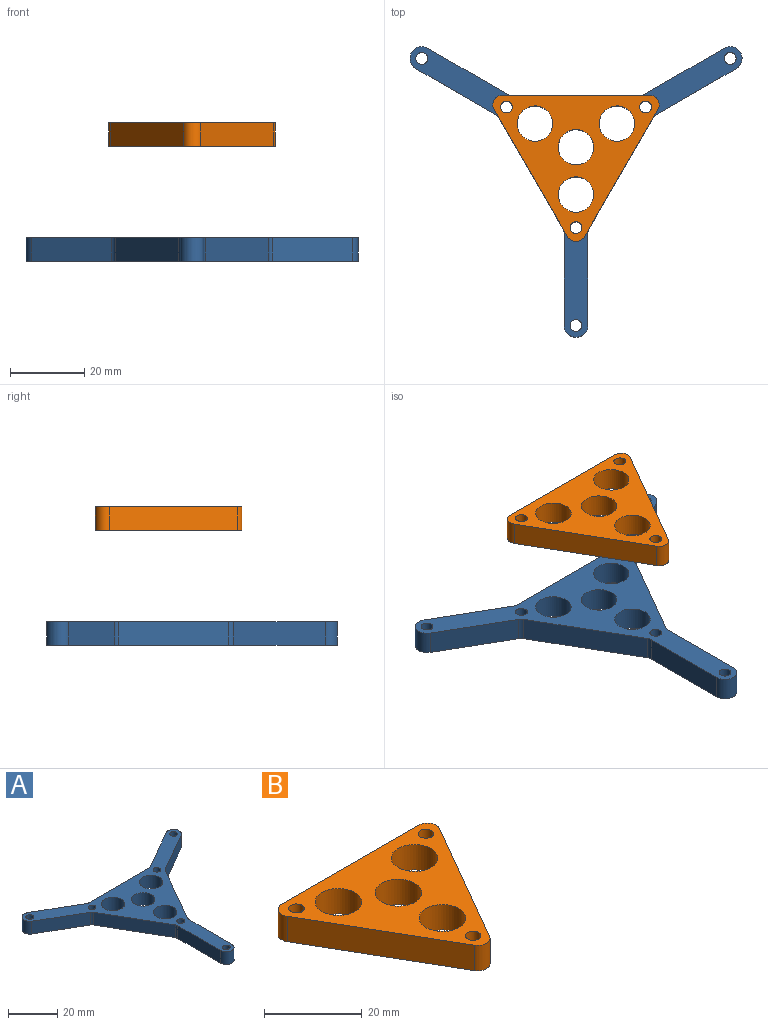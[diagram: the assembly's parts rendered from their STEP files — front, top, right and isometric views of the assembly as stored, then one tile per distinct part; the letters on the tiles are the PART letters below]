
ASSEMBLY  parts=2 mates=2
PART A: 30 faces, bbox 89.2x78.1x6.4 mm
  f0: plane 24.72x6.35mm, normal (1,0,0), area 157mm2, adj f19,f22,f23,f25
  f1: plane 29.73x17.17mm, normal (0.87,-0.5,0), area 218mm2, adj f22,f23,f25,f29
  f2: plane 21.41x12.36mm, normal (0.5,-0.87,0), area 157mm2, adj f3,f22,f23,f29
  f3: cylinder r=3.17mm len=6.35mm, axis (0,0,-1), area 63.3mm2, adj f2,f4,f22,f23
  f4: plane 21.41x12.36mm, normal (-0.5,0.87,0), area 157mm2, adj f3,f22,f23,f28
  f5: plane 34.33x6.35mm, normal (0,1,0), area 218mm2, adj f22,f23,f27,f28
  f6: plane 21.41x12.36mm, normal (0.5,0.87,0), area 157mm2, adj f7,f22,f23,f27
  f7: cylinder r=3.17mm len=6.35mm, axis (0,0,-1), area 63.3mm2, adj f6,f8,f22,f23
  f8: plane 21.41x12.36mm, normal (-0.5,-0.87,0), area 157mm2, adj f7,f22,f23,f26
  f9: plane 29.73x17.17mm, normal (-0.87,-0.5,0), area 218mm2, adj f22,f23,f24,f26
  f10: plane 24.72x6.35mm, normal (-1,0,0), area 157mm2, adj f19,f22,f23,f24
  f11: cylinder r=1.59mm len=6.35mm, axis (0,0,-1), area 63.3mm2, adj f22,f23
  f12: cylinder r=1.59mm len=6.35mm, axis (0,0,-1), area 63.3mm2, adj f22,f23
  f13: cylinder r=1.59mm len=6.35mm, axis (0,0,-1), area 63.3mm2, adj f22,f23
  f14: cylinder r=4.76mm len=9.53mm, axis (0,0,-1), area 190mm2, adj f22,f23
  f15: cylinder r=4.76mm len=9.53mm, axis (0,0,-1), area 190mm2, adj f22,f23
  f16: cylinder r=4.76mm len=9.53mm, axis (0,0,-1), area 190mm2, adj f22,f23
  f17: cylinder r=1.59mm len=6.35mm, axis (0,0,-1), area 63.3mm2, adj f22,f23
  f18: cylinder r=1.59mm len=6.35mm, axis (0,0,-1), area 63.3mm2, adj f22,f23
  f19: cylinder r=3.17mm len=6.35mm, axis (0,0,-1), area 63.3mm2, adj f0,f10,f22,f23
  f20: cylinder r=1.59mm len=6.35mm, axis (0,0,-1), area 63.3mm2, adj f22,f23
  f21: cylinder r=4.76mm len=9.53mm, axis (0,0,-1), area 190mm2, adj f22,f23
  f22: plane 89.21x78.11mm, normal (0,0,1), area 1160.8mm2, adj f0,f1,f2,f3,f4,f5,f6,f7
  f23: plane 89.21x78.11mm, normal (0,0,-1), area 1160.8mm2, adj f0,f1,f2,f3,f4,f5,f6,f7
  f24: cylinder r=2.54mm len=6.35mm, axis (0,0,-1), area 8.4mm2, adj f9,f10,f22,f23
  f25: cylinder r=2.54mm len=6.35mm, axis (0,0,-1), area 8.4mm2, adj f0,f1,f22,f23
  f26: cylinder r=2.54mm len=6.35mm, axis (0,0,-1), area 8.4mm2, adj f8,f9,f22,f23
  f27: cylinder r=2.54mm len=6.35mm, axis (0,0,-1), area 8.4mm2, adj f5,f6,f22,f23
  f28: cylinder r=2.54mm len=6.35mm, axis (0,0,-1), area 8.4mm2, adj f4,f5,f22,f23
  f29: cylinder r=2.54mm len=6.35mm, axis (0,0,-1), area 8.4mm2, adj f1,f2,f22,f23
PART B: 15 faces, bbox 44.7x39.4x6.4 mm
  f0: plane 34.29x19.8mm, normal (-0.87,-0.5,0), area 251.4mm2, adj f10,f11,f12,f14
  f1: plane 34.29x19.8mm, normal (0.87,-0.5,0), area 251.4mm2, adj f10,f11,f12,f13
  f2: cylinder r=1.59mm len=6.35mm, axis (0,0,-1), area 63.3mm2, adj f10,f11
  f3: cylinder r=1.59mm len=6.35mm, axis (0,0,-1), area 63.3mm2, adj f10,f11
  f4: cylinder r=1.59mm len=6.35mm, axis (0,0,-1), area 63.3mm2, adj f10,f11
  f5: cylinder r=4.76mm len=9.53mm, axis (0,0,-1), area 190mm2, adj f10,f11
  f6: cylinder r=4.76mm len=9.53mm, axis (0,0,-1), area 190mm2, adj f10,f11
  f7: cylinder r=4.76mm len=9.53mm, axis (0,0,-1), area 190mm2, adj f10,f11
  f8: plane 39.59x6.35mm, normal (0,1,0), area 251.4mm2, adj f10,f11,f13,f14
  f9: cylinder r=4.76mm len=9.53mm, axis (0,0,-1), area 190mm2, adj f10,f11
  f10: plane 44.67x39.37mm, normal (0,0,1), area 692.1mm2, adj f0,f1,f2,f3,f4,f5,f6,f7
  f11: plane 44.67x39.37mm, normal (0,0,-1), area 692.1mm2, adj f0,f1,f2,f3,f4,f5,f6,f7
  f12: cylinder r=2.54mm len=6.35mm, axis (0,0,-1), area 33.8mm2, adj f0,f1,f10,f11
  f13: cylinder r=2.54mm len=6.35mm, axis (0,0,-1), area 33.8mm2, adj f1,f8,f10,f11
  f14: cylinder r=2.54mm len=6.35mm, axis (0,0,-1), area 33.8mm2, adj f0,f8,f10,f11
PLACE A t=(0.8,70.33,-3.78)mm
PLACE B t=(0.8,70.33,27.07)mm
MATE parallel A.f21 <-> B.f11  axis (0,0,1) through (0.8,70.33,2.57)mm
MATE cylindrical B.f5 <-> A.f14  axis (0,0,-1) through (-10.2,76.68,33.42)mm
